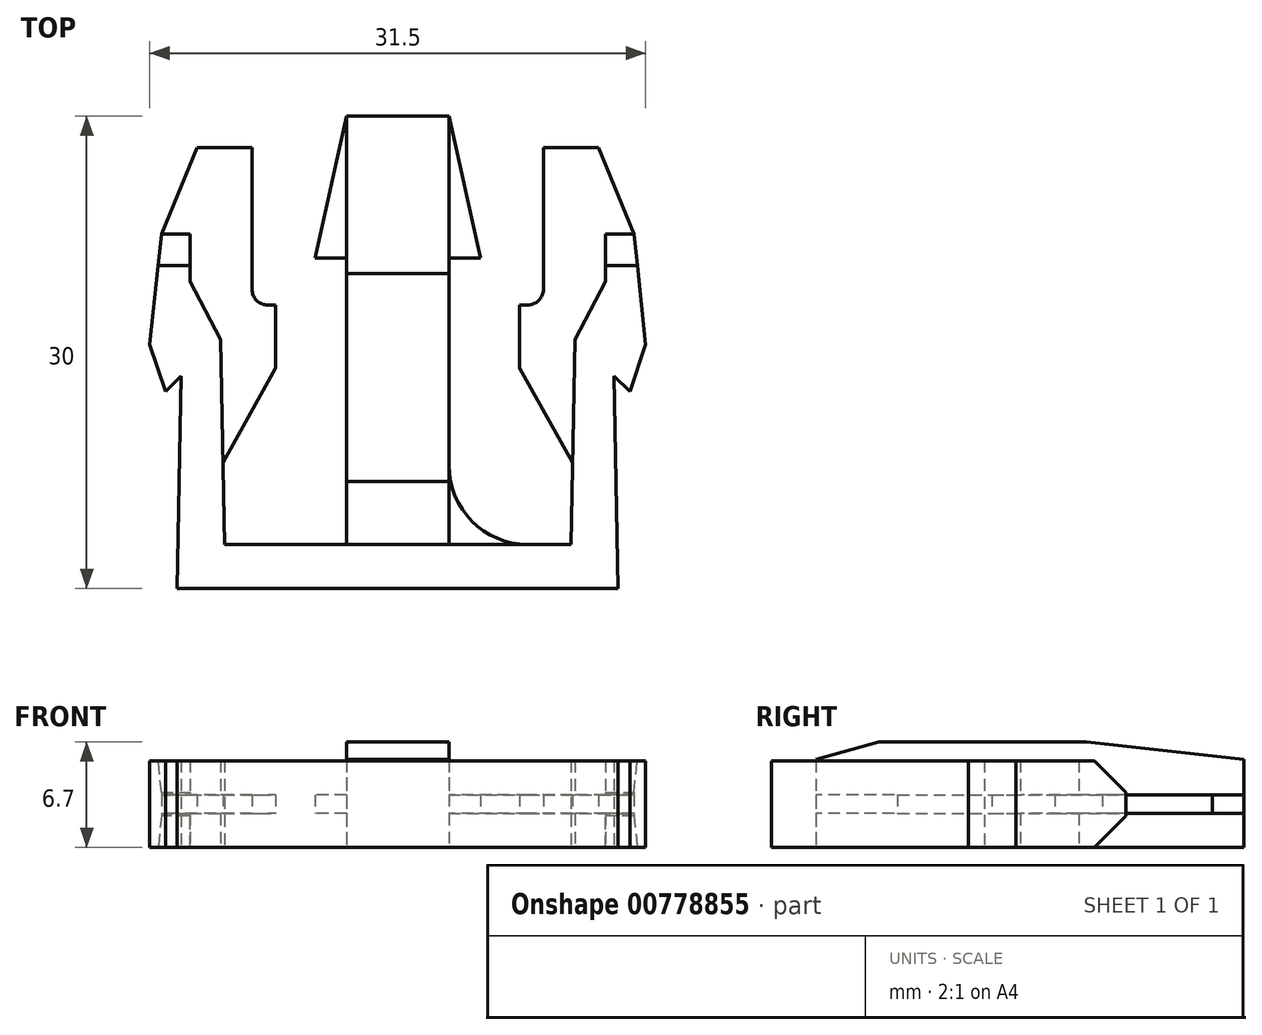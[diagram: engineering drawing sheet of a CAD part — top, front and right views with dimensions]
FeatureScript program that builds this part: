
annotation { "Feature Type Name" : "Feature", "Feature Type Description" : "" }
export const myFeature = defineFeature(function(context is Context, id is Id, definition is map)
    precondition{}
    {
        {
            var Q0;
            Q0=qCreatedBy(makeId("Top.planeOp"),FACE);
            var sketch = newSketch(context, id + "F0", { "sketchPlane" : qUnion([Q0])});
            skLineSegment(sketch, "E0", {"start": v(0, 30) * mm, "end": v(-3.25, 30) * mm});
            skLineSegment(sketch, "E1", {"start": v(-3.25, 30) * mm, "end": v(-3.25, 7.8) * mm});
            skLineSegment(sketch, "E2", {"start": v(0, 2.8) * mm, "end": v(-3.25, 2.8) * mm});
            skPoint(sketch, "E3.start.orphan", {"position": v(-3.25, 0) * mm});
            skLineSegment(sketch, "E4", {"start": v(-14, 0) * mm, "end": v(-13.75, 13.5) * mm});
            skLineSegment(sketch, "E5", {"start": v(0, 0) * mm, "end": v(-14, 0) * mm});
            skLineSegment(sketch, "E6", {"start": v(-11, 2.8) * mm, "end": v(-11.25, 15.8) * mm});
            skLineSegment(sketch, "E7", {"start": v(-13.75, 13.5) * mm, "end": v(-14.75, 12.5) * mm});
            skLineSegment(sketch, "E8", {"start": v(-14.75, 12.5) * mm, "end": v(-15.75, 15.5) * mm});
            skLineSegment(sketch, "E9", {"start": v(-15.75, 15.5) * mm, "end": v(-15, 22.5) * mm});
            skLineSegment(sketch, "E10", {"start": v(-15, 22.5) * mm, "end": v(-13.2, 22.5) * mm});
            skLineSegment(sketch, "E11", {"start": v(-13.2, 22.5) * mm, "end": v(-13.2, 19.5) * mm});
            skLineSegment(sketch, "E12", {"start": v(-13.2, 19.5) * mm, "end": v(-11.25, 15.8) * mm});
            skLineSegment(sketch, "E13", {"start": v(-11.1, 8) * mm, "end": v(-7.75, 14) * mm});
            skLineSegment(sketch, "E14", {"start": v(-7.75, 14) * mm, "end": v(-7.75, 18) * mm});
            skLineSegment(sketch, "E15", {"start": v(-9.25, 19) * mm, "end": v(-9.25, 28) * mm});
            skLineSegment(sketch, "E16", {"start": v(-9.25, 28) * mm, "end": v(-12.75, 28) * mm});
            skLineSegment(sketch, "E17", {"start": v(-12.75, 28) * mm, "end": v(-15, 22.5) * mm});
            skLineSegment(sketch, "E18", {"start": v(-7.75, 18) * mm, "end": v(-8.25, 18) * mm});
            skPoint(sketch, "E19.visualSharp", {"position": v(-9.25, 18) * mm});
            skArc(sketch, "E19.filletArc", {"start": v(-9.25, 19) * mm, "mid": v(-8.96, 18.3) * mm, "end": v(-8.25, 18) * mm});
            skPoint(sketch, "E20", {"position": v(-8.25, 2.8) * mm});
            skPoint(sketch, "E21", {"position": v(-3.25, 7.8) * mm});
            skPoint(sketch, "E22.orphan", {"position": v(-3.25, 2.8) * mm});
            skLineSegment(sketch, "E23.trimOffspring", {"start": v(-8.25, 2.8) * mm, "end": v(-11, 2.8) * mm});
            skArc(sketch, "E24", {"start": v(-3.25, 7.8) * mm, "mid": v(-4.71, 4.26) * mm, "end": v(-8.25, 2.8) * mm});
            skLineSegment(sketch, "E25", {"start": v(-3.25, 7.8) * mm, "end": v(-3.25, 2.8) * mm});
            skLineSegment(sketch, "E26", {"start": v(-8.25, 2.8) * mm, "end": v(-3.25, 2.8) * mm});
            skLineSegment(sketch, "E27", {"start": v(-3.25, 30) * mm, "end": v(-5.25, 21) * mm});
            skLineSegment(sketch, "E28", {"start": v(-5.25, 21) * mm, "end": v(-3.25, 21) * mm});
            skLineSegment(sketch, "E29.MirrorCS", {"start": v(0, 30) * mm, "end": v(3.25, 30) * mm});
            skLineSegment(sketch, "E30.MirrorCS", {"start": v(3.25, 30) * mm, "end": v(3.25, 7.8) * mm});
            skLineSegment(sketch, "E31.MirrorCS", {"start": v(3.25, 7.8) * mm, "end": v(3.25, 2.8) * mm});
            skLineSegment(sketch, "E32.MirrorCS", {"start": v(8.25, 2.8) * mm, "end": v(3.25, 2.8) * mm});
            skLineSegment(sketch, "E33.MirrorCS", {"start": v(8.25, 2.8) * mm, "end": v(11, 2.8) * mm});
            skLineSegment(sketch, "E34.MirrorCS", {"start": v(11, 2.8) * mm, "end": v(11.25, 15.8) * mm});
            skLineSegment(sketch, "E35.MirrorCS", {"start": v(13.2, 19.5) * mm, "end": v(11.25, 15.8) * mm});
            skLineSegment(sketch, "E36.MirrorCS", {"start": v(13.2, 22.5) * mm, "end": v(13.2, 19.5) * mm});
            skLineSegment(sketch, "E37.MirrorCS", {"start": v(15, 22.5) * mm, "end": v(13.2, 22.5) * mm});
            skLineSegment(sketch, "E38.MirrorCS", {"start": v(15.75, 15.5) * mm, "end": v(15, 22.5) * mm});
            skLineSegment(sketch, "E39.MirrorCS", {"start": v(14.75, 12.5) * mm, "end": v(15.75, 15.5) * mm});
            skLineSegment(sketch, "E40.MirrorCS", {"start": v(13.75, 13.5) * mm, "end": v(14.75, 12.5) * mm});
            skLineSegment(sketch, "E41.MirrorCS", {"start": v(14, 0) * mm, "end": v(13.75, 13.5) * mm});
            skLineSegment(sketch, "E42.MirrorCS", {"start": v(0, 0) * mm, "end": v(14, 0) * mm});
            skArc(sketch, "E43.MirrorCS", {"start": v(3.25, 7.8) * mm, "mid": v(4.71, 4.26) * mm, "end": v(8.25, 2.8) * mm});
            skLineSegment(sketch, "E44.MirrorCS", {"start": v(5.25, 21) * mm, "end": v(3.25, 21) * mm});
            skLineSegment(sketch, "E45.MirrorCS", {"start": v(3.25, 30) * mm, "end": v(5.25, 21) * mm});
            skLineSegment(sketch, "E46.MirrorCS", {"start": v(11.1, 8) * mm, "end": v(7.75, 14) * mm});
            skLineSegment(sketch, "E47.MirrorCS", {"start": v(7.75, 14) * mm, "end": v(7.75, 18) * mm});
            skLineSegment(sketch, "E48.MirrorCS", {"start": v(9.25, 19) * mm, "end": v(9.25, 28) * mm});
            skLineSegment(sketch, "E49.MirrorCS", {"start": v(7.75, 18) * mm, "end": v(8.25, 18) * mm});
            skArc(sketch, "E50.MirrorCS", {"start": v(9.25, 19) * mm, "mid": v(8.96, 18.3) * mm, "end": v(8.25, 18) * mm});
            skLineSegment(sketch, "E51.MirrorCS", {"start": v(9.25, 28) * mm, "end": v(12.75, 28) * mm});
            skLineSegment(sketch, "E52.MirrorCS", {"start": v(12.75, 28) * mm, "end": v(15, 22.5) * mm});
            skSolve(sketch);
        }
        {
            var Q0;
            {var subQ6=sQuery(id+"F0.wireOp",EDGE,"E0");Q0=makeQuery(id+"F0.imprint","IMPRINT",FACE,{"disambiguationData":[TD([[makeQuery(id+"F0.imprint","IMPRINT",EDGE,{"derivedFrom":subQ6}),1.0]])]});}
            extrude(context, id + "F1", {"entities" : qUnion([Q0]), "depth" : 5.5 * mm, "offsetDistance" : 25 * mm, "symmetric" : true});
        }
        {
            var Q0;
            Q0=makeQuery(id+"F0.imprint","IMPRINT",FACE,{"disambiguationData":[TD([[makeQuery(id+"F0.imprint","IMPRINT",EDGE,{"derivedFrom":sQuery(id+"F0.wireOp",EDGE,"E10")}),1.0]])]});
            var Q1;
            {var subQ0=sQuery(id+"F0.wireOp",EDGE,"E27");Q1=makeQuery(id+"F0.imprint","IMPRINT",FACE,{"disambiguationData":[TD([[makeQuery(id+"F0.imprint","IMPRINT",EDGE,{"derivedFrom":subQ0}),1.0]])]});}
            var Q2;
            {var subQ2=sQuery(id+"F0.wireOp",EDGE,"E44.MirrorCS");Q2=makeQuery(id+"F0.imprint","IMPRINT",FACE,{"disambiguationData":[TD([[makeQuery(id+"F0.imprint","IMPRINT",EDGE,{"derivedFrom":subQ2}),-1.0]])]});}
            var Q3;
            {var subQ0=sQuery(id+"F0.wireOp",EDGE,"E35.MirrorCS");Q3=makeQuery(id+"F0.imprint","IMPRINT",FACE,{"disambiguationData":[TD([[makeQuery(id+"F0.imprint","IMPRINT",EDGE,{"derivedFrom":subQ0}),-1.0]])]});}
            var Q4;
            Q4=makeQuery(id+"F0.imprint","IMPRINT",FACE,{"disambiguationData":[TD([[makeQuery(id+"F0.imprint","IMPRINT",EDGE,{"derivedFrom":sQuery(id+"F0.wireOp",EDGE,"E31.MirrorCS")}),1.0]])]});
            var Q5;
            Q5=makeQuery(id+"F0.imprint","IMPRINT",FACE,{"disambiguationData":[TD([[makeQuery(id+"F0.imprint","IMPRINT",EDGE,{"derivedFrom":sQuery(id+"F0.wireOp",EDGE,"E24")}),1.0]])]});
            extrude(context, id + "F2", {"entities" : qUnion([Q0, Q1, Q2, Q3, Q4, Q5]), "operationType" : NewBodyOperationType.ADD, "depth" : 1.2 * mm, "offsetDistance" : 25 * mm, "symmetric" : true});
        }
        {
            var Q0;
            Q0=makeQuery(id+"F1.opExtrude","CAP_EDGE",EDGE,{"disambiguationData":[OSD([sQuery(id+"F0.wireOp",EDGE,"E37.MirrorCS")])],"isStart":false});
            var Q1;
            Q1=makeQuery(id+"F1.opExtrude","CAP_EDGE",EDGE,{"disambiguationData":[OSD([sQuery(id+"F0.wireOp",EDGE,"E37.MirrorCS")])],"isStart":true});
            var Q2;
            Q2=makeQuery(id+"F1.opExtrude","CAP_EDGE",EDGE,{"disambiguationData":[OSD([sQuery(id+"F0.wireOp",EDGE,"E10")])],"isStart":false});
            var Q3;
            Q3=makeQuery(id+"F1.opExtrude","CAP_EDGE",EDGE,{"disambiguationData":[OSD([sQuery(id+"F0.wireOp",EDGE,"E10")])],"isStart":true});
            chamfer(context, id + "F3", {"entities" : qUnion([Q0, Q1, Q2, Q3]), "width" : 2 * mm, "tangentPropagation" : true});
        }
        {
            var Q0;
            Q0=makeQuery(id+"F1.opExtrude","CAP_FACE",FACE,{"disambiguationData":[OSD([sQuery(id+"F0.wireOp",EDGE,"E0"),sQuery(id+"F0.wireOp",EDGE,"E1"),sQuery(id+"F0.wireOp",EDGE,"E4"),sQuery(id+"F0.wireOp",EDGE,"E5"),sQuery(id+"F0.wireOp",EDGE,"E6"),sQuery(id+"F0.wireOp",EDGE,"E7"),sQuery(id+"F0.wireOp",EDGE,"E8"),sQuery(id+"F0.wireOp",EDGE,"E9"),sQuery(id+"F0.wireOp",EDGE,"E10"),sQuery(id+"F0.wireOp",EDGE,"E11"),sQuery(id+"F0.wireOp",EDGE,"E12"),sQuery(id+"F0.wireOp",EDGE,"E23.trimOffspring"),sQuery(id+"F0.wireOp",EDGE,"E25"),sQuery(id+"F0.wireOp",EDGE,"E26"),sQuery(id+"F0.wireOp",EDGE,"E29.MirrorCS"),sQuery(id+"F0.wireOp",EDGE,"E30.MirrorCS"),sQuery(id+"F0.wireOp",EDGE,"E31.MirrorCS"),sQuery(id+"F0.wireOp",EDGE,"E32.MirrorCS"),sQuery(id+"F0.wireOp",EDGE,"E33.MirrorCS"),sQuery(id+"F0.wireOp",EDGE,"E34.MirrorCS"),sQuery(id+"F0.wireOp",EDGE,"E35.MirrorCS"),sQuery(id+"F0.wireOp",EDGE,"E36.MirrorCS"),sQuery(id+"F0.wireOp",EDGE,"E37.MirrorCS"),sQuery(id+"F0.wireOp",EDGE,"E38.MirrorCS"),sQuery(id+"F0.wireOp",EDGE,"E39.MirrorCS"),sQuery(id+"F0.wireOp",EDGE,"E40.MirrorCS"),sQuery(id+"F0.wireOp",EDGE,"E41.MirrorCS"),sQuery(id+"F0.wireOp",EDGE,"E42.MirrorCS")])],"isStart":false});
            var sketch = newSketch(context, id + "F4", { "sketchPlane" : qUnion([Q0])});
            skLineSegment(sketch, "E53.bottom", {"start": v(-3.25, 30) * mm, "end": v(3.25, 30) * mm});
            skLineSegment(sketch, "E53.top", {"start": v(-3.25, 2.8) * mm, "end": v(3.25, 2.8) * mm});
            skLineSegment(sketch, "E53.left", {"start": v(-3.25, 30) * mm, "end": v(-3.25, 2.8) * mm});
            skLineSegment(sketch, "E53.right", {"start": v(3.25, 30) * mm, "end": v(3.25, 2.8) * mm});
            skSolve(sketch);
        }
        {
            var Q0;
            Q0=makeQuery(id+"F4.imprint","IMPRINT",FACE,{"disambiguationData":[TD([[makeQuery(id+"F4.imprint","IMPRINT",EDGE,{"derivedFrom":sQuery(id+"F4.wireOp",EDGE,"E53.bottom")}),-1.0]])]});
            extrude(context, id + "F5", {"entities" : qUnion([Q0]), "operationType" : NewBodyOperationType.ADD, "depth" : 1.2 * mm, "offsetDistance" : 25 * mm});
        }
        {
            var Q0;
            Q0=makeQuery(id+"F5.opExtrude","CAP_EDGE",EDGE,{"disambiguationData":[OSD([sQuery(id+"F4.wireOp",EDGE,"E53.top")])],"isStart":false});
            chamfer(context, id + "F6", {"entities" : qUnion([Q0]), "chamferType" : ChamferType.TWO_OFFSETS, "width1" : 4 * mm, "oppositeDirection" : false, "width2" : 1.1 * mm, "tangentPropagation" : true});
        }
        {
            var Q0;
            Q0=makeQuery(id+"F5.opExtrude","CAP_EDGE",EDGE,{"disambiguationData":[OSD([sQuery(id+"F4.wireOp",EDGE,"E53.bottom")])],"isStart":false});
            chamfer(context, id + "F7", {"entities" : qUnion([Q0]), "chamferType" : ChamferType.TWO_OFFSETS, "width1" : 1.1 * mm, "oppositeDirection" : false, "width2" : 10 * mm, "tangentPropagation" : true});
        }
    });
